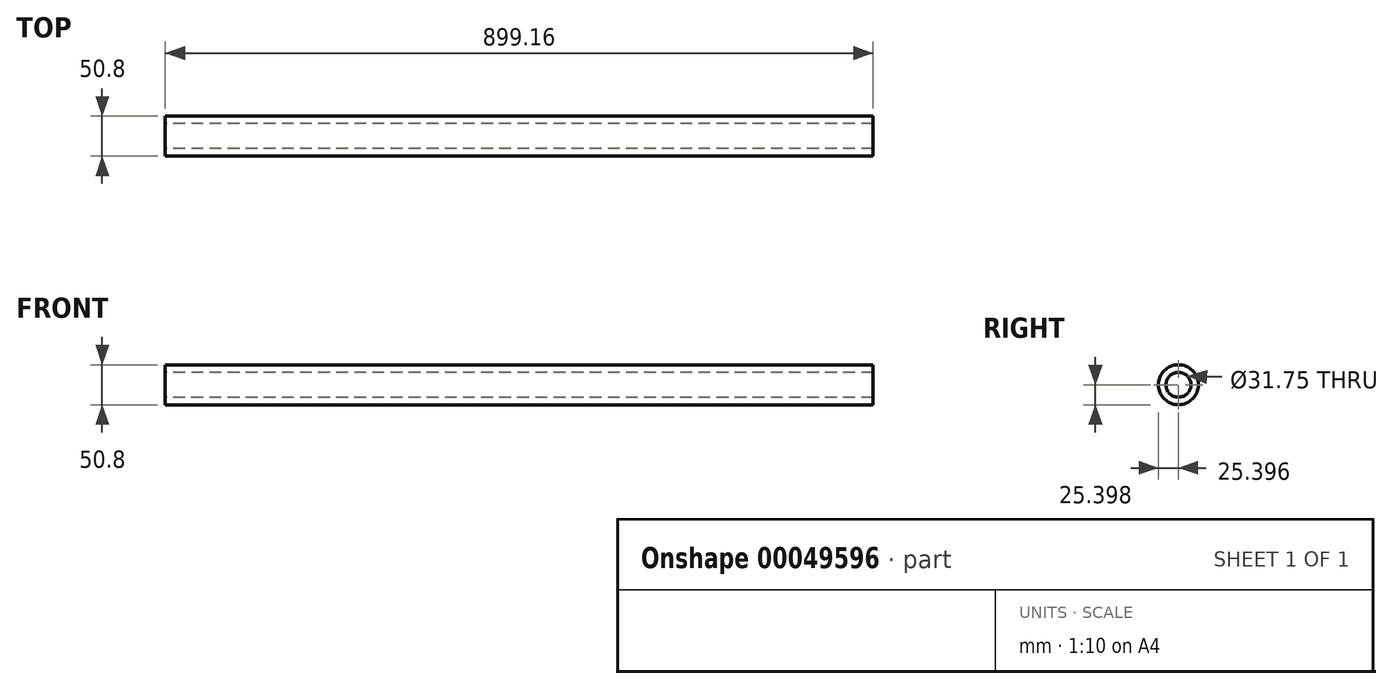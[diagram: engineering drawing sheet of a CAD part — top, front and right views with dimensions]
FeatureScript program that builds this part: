
annotation { "Feature Type Name" : "Feature", "Feature Type Description" : "" }
export const myFeature = defineFeature(function(context is Context, id is Id, definition is map)
    precondition{}
    {
        {
            var Q0;
            Q0=qCreatedBy(makeId("Right.planeOp"),FACE);
            var sketch = newSketch(context, id + "F0", { "sketchPlane" : qUnion([Q0])});
            skCircle(sketch, "E0", {"center": v(-17.56, 18.35) * mm, "radius": 25.4 * mm});
            skCircle(sketch, "E1", {"center": v(-17.56, 18.35) * mm, "radius": 15.88 * mm});
            skSolve(sketch);
        }
        {
            var Q0;
            Q0=makeQuery(id+"F0.imprint","IMPRINT",FACE,{"disambiguationData":[TD([[makeQuery(id+"F0.imprint","IMPRINT",EDGE,{"derivedFrom":sQuery(id+"F0.wireOp",EDGE,"E0")}),1.0]])]});
            extrude(context, id + "F1", {"entities" : qUnion([Q0]), "depth" : 899.16 * mm});
        }
    });
